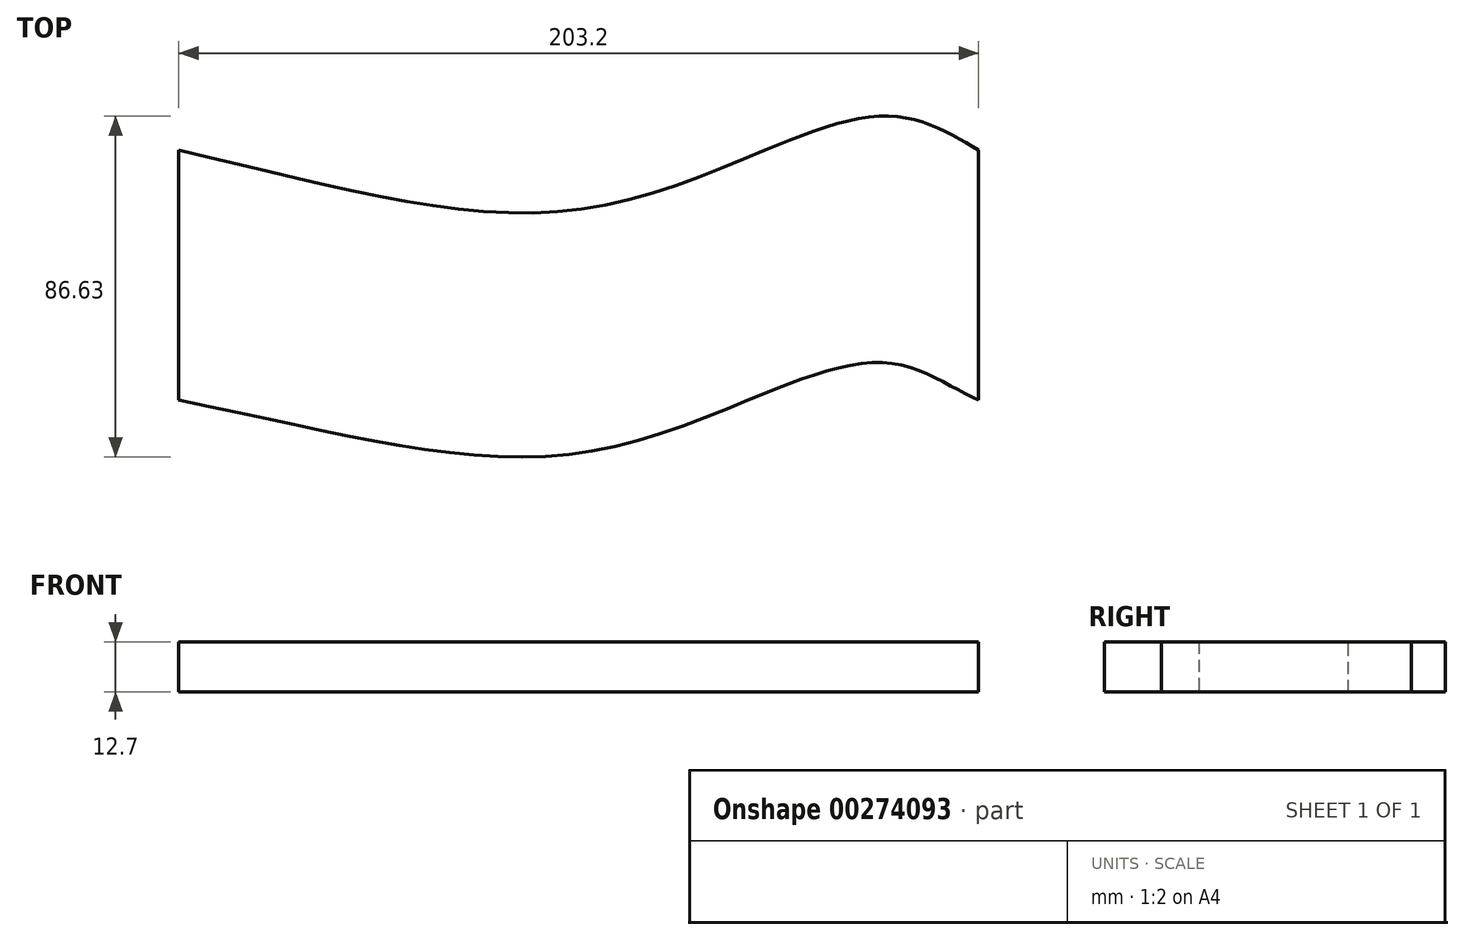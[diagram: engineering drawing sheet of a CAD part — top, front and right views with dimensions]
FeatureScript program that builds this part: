
annotation { "Feature Type Name" : "Feature", "Feature Type Description" : "" }
export const myFeature = defineFeature(function(context is Context, id is Id, definition is map)
    precondition{}
    {
        {
            var Q0;
            Q0=qCreatedBy(makeId("Top.planeOp"),FACE);
            var sketch = newSketch(context, id + "F0", { "sketchPlane" : qUnion([Q0])});
            skLineSegment(sketch, "E0", {"start": v(-57.89, 53.93) * mm, "end": v(-57.89, -9.57) * mm});
            skLineSegment(sketch, "E1", {"start": v(145.31, -9.57) * mm, "end": v(145.31, 53.93) * mm});
            skLineSegment(sketch, "E2", {"start": v(-57.89, -9.57) * mm, "end": v(145.31, -9.57) * mm});
            skFitSpline(sketch, "E3", {"points": [v(-57.89, -9.57) * mm, v(50.35, -21.93) * mm, v(119.88, 0) * mm, v(145.31, -9.57) * mm], "startDerivative": vector(294.44, -59.23) * mm, "endDerivative": vector(97.6, -41.66) * mm});
            skFitSpline(sketch, "E4", {"points": [v(-57.89, 53.93) * mm, v(50.35, 39.92) * mm, v(119.88, 62.6) * mm, v(145.31, 53.93) * mm], "startDerivative": vector(294.09, -67.94) * mm, "endDerivative": vector(95.95, -56.65) * mm});
            skLineSegment(sketch, "E5", {"start": v(-57.89, 53.93) * mm, "end": v(145.31, 53.93) * mm});
            skSolve(sketch);
        }
        {
            var Q0;
            {var subQ0=sQuery(id+"F0.wireOp",EDGE,"E3");var subQ1=sQuery(id+"F0.wireOp",EDGE,"E2");var subQ3=makeQuery(id+"F0.imprint","INTERSECT",VERTEX,{"derivedFrom":[subQ1,subQ0]});Q0=makeQuery(id+"F0.imprint","IMPRINT",FACE,{"disambiguationData":[TD([[makeQuery(id+"F0.imprint","IMPRINT",EDGE,{"disambiguationData":[TD([[subQ3,1.0]])],"derivedFrom":subQ1}),-1.0]])]});}
            var Q1;
            {var subQ4=sQuery(id+"F0.wireOp",EDGE,"E0");Q1=makeQuery(id+"F0.imprint","IMPRINT",FACE,{"disambiguationData":[TD([[makeQuery(id+"F0.imprint","IMPRINT",EDGE,{"derivedFrom":subQ4}),1.0]])]});}
            var Q2;
            {var subQ0=sQuery(id+"F0.wireOp",EDGE,"E5");var subQ1=sQuery(id+"F0.wireOp",EDGE,"E4");var subQ3=makeQuery(id+"F0.imprint","INTERSECT",VERTEX,{"derivedFrom":[subQ1,subQ0]});Q2=makeQuery(id+"F0.imprint","IMPRINT",FACE,{"disambiguationData":[TD([[makeQuery(id+"F0.imprint","IMPRINT",EDGE,{"disambiguationData":[TD([[subQ3,-1.0]])],"derivedFrom":subQ1}),-1.0]])]});}
            extrude(context, id + "F1", {"entities" : qUnion([Q0, Q1, Q2]), "depth" : 12.7 * mm});
        }
    });
